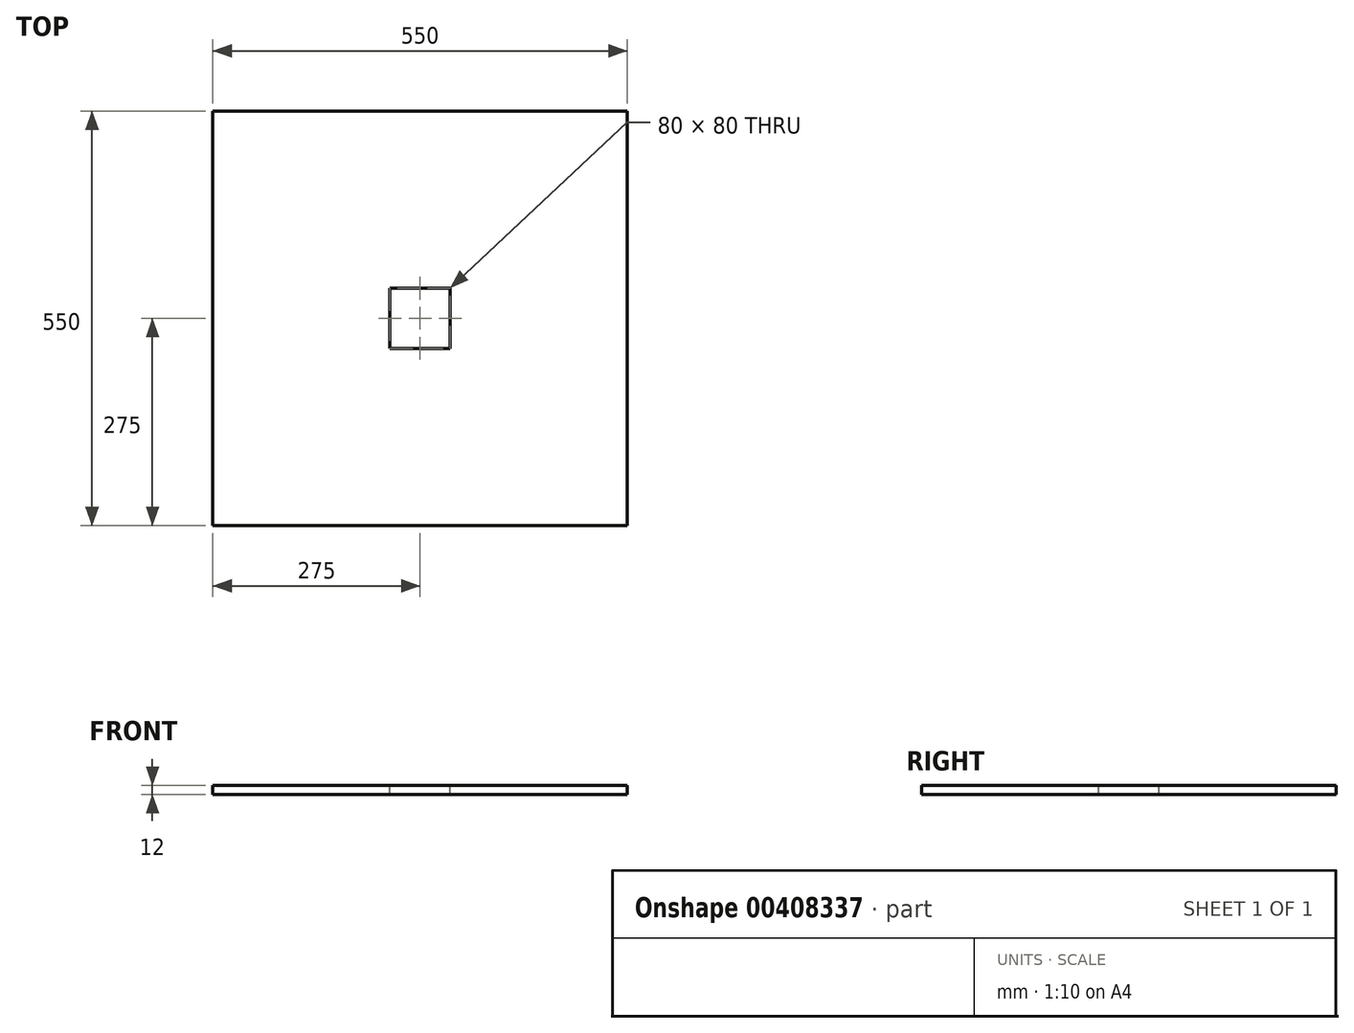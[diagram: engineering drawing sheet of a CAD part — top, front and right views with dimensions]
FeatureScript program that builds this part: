
annotation { "Feature Type Name" : "Feature", "Feature Type Description" : "" }
export const myFeature = defineFeature(function(context is Context, id is Id, definition is map)
    precondition{}
    {
        {
            var Q0;
            Q0=qCreatedBy(makeId("Top.planeOp"),FACE);
            var sketch = newSketch(context, id + "F0", { "sketchPlane" : qUnion([Q0])});
            skLineSegment(sketch, "E0.bottom", {"start": v(275, 275) * mm, "end": v(-275, 275) * mm});
            skLineSegment(sketch, "E0.top", {"start": v(275, -275) * mm, "end": v(-275, -275) * mm});
            skLineSegment(sketch, "E0.left", {"start": v(275, 275) * mm, "end": v(275, -275) * mm});
            skLineSegment(sketch, "E0.right", {"start": v(-275, 275) * mm, "end": v(-275, -275) * mm});
            skPoint(sketch, "E0.middle", {"position": v(0, 0) * mm});
            skSolve(sketch);
        }
        {
            var Q0;
            Q0=makeQuery(id+"F0.imprint","IMPRINT",FACE,{"disambiguationData":[TD([[makeQuery(id+"F0.imprint","IMPRINT",EDGE,{"derivedFrom":sQuery(id+"F0.wireOp",EDGE,"E0.bottom")}),1.0]])]});
            extrude(context, id + "F1", {"entities" : qUnion([Q0]), "depth" : 12 * mm});
        }
        {
            var Q0;
            Q0=makeQuery(id+"F1.opExtrude","CAP_FACE",FACE,{"disambiguationData":[OSD([sQuery(id+"F0.wireOp",EDGE,"E0.bottom"),sQuery(id+"F0.wireOp",EDGE,"E0.top"),sQuery(id+"F0.wireOp",EDGE,"E0.left"),sQuery(id+"F0.wireOp",EDGE,"E0.right")])],"isStart":false});
            var sketch = newSketch(context, id + "F2", { "sketchPlane" : qUnion([Q0])});
            skLineSegment(sketch, "E1.bottom", {"start": v(40, 40) * mm, "end": v(-40, 40) * mm});
            skLineSegment(sketch, "E1.top", {"start": v(40, -40) * mm, "end": v(-40, -40) * mm});
            skLineSegment(sketch, "E1.left", {"start": v(40, 40) * mm, "end": v(40, -40) * mm});
            skLineSegment(sketch, "E1.right", {"start": v(-40, 40) * mm, "end": v(-40, -40) * mm});
            skPoint(sketch, "E1.middle", {"position": v(0, 0) * mm});
            skSolve(sketch);
        }
        {
            var Q0;
            Q0=makeQuery(id+"F2.imprint","IMPRINT",FACE,{"disambiguationData":[TD([[makeQuery(id+"F2.imprint","IMPRINT",EDGE,{"derivedFrom":sQuery(id+"F2.wireOp",EDGE,"E1.bottom")}),1.0]])]});
            extrude(context, id + "F3", {"entities" : qUnion([Q0]), "operationType" : NewBodyOperationType.REMOVE, "endBound" : BoundingType.UP_TO_NEXT, "oppositeDirection" : true, "depth" : 25 * mm});
        }
    });
